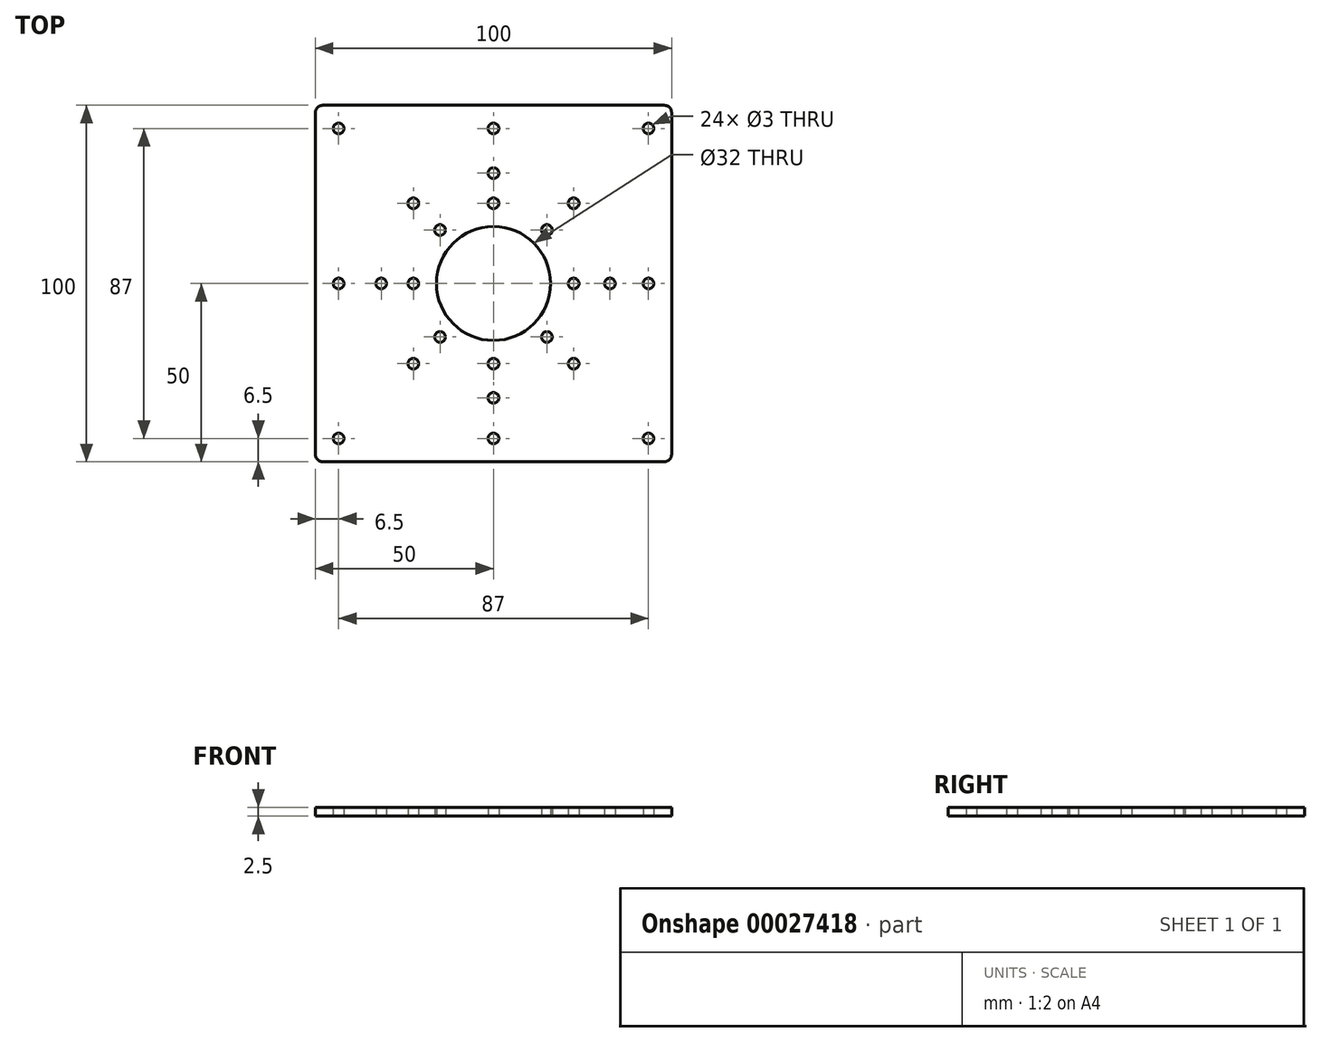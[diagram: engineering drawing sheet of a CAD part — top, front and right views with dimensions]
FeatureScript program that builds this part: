
annotation { "Feature Type Name" : "Feature", "Feature Type Description" : "" }
export const myFeature = defineFeature(function(context is Context, id is Id, definition is map)
    precondition{}
    {
        {
            var Q0;
            Q0=qCreatedBy(makeId("Top.planeOp"),FACE);
            var sketch = newSketch(context, id + "F0", { "sketchPlane" : qUnion([Q0])});
            skLineSegment(sketch, "E0.rect.bottom", {"start": v(50, -50) * mm, "end": v(-50, -50) * mm});
            skLineSegment(sketch, "E0.rect.top", {"start": v(50, 50) * mm, "end": v(-50, 50) * mm});
            skLineSegment(sketch, "E0.rect.left", {"start": v(50, -50) * mm, "end": v(50, 50) * mm});
            skLineSegment(sketch, "E0.rect.right", {"start": v(-50, -50) * mm, "end": v(-50, 50) * mm});
            skPoint(sketch, "E0.rect.middle", {"position": v(0, 0) * mm});
            skCircle(sketch, "E1", {"center": v(0, 0) * mm, "radius": 16 * mm});
            skLineSegment(sketch, "E2", {"start": v(50, 45) * mm, "end": v(-50, 45) * mm, "construction": true});
            skLineSegment(sketch, "E3", {"start": v(-50, 0) * mm, "end": v(50, 0) * mm, "construction": true});
            skLineSegment(sketch, "E4", {"start": v(45, 50) * mm, "end": v(45, -50) * mm, "construction": true});
            skCircle(sketch, "E5", {"center": v(-43.5, -43.5) * mm, "radius": 1.5 * mm});
            skCircle(sketch, "E6.MirrorC", {"center": v(43.5, -43.5) * mm, "radius": 1.5 * mm});
            skCircle(sketch, "E7.MirrorC", {"center": v(43.5, 43.5) * mm, "radius": 1.5 * mm});
            skCircle(sketch, "E8.MirrorC", {"center": v(-43.5, 43.5) * mm, "radius": 1.5 * mm});
            skPoint(sketch, "E9.centerSnap0", {"position": v(0, 45) * mm});
            skLineSegment(sketch, "E10.rect.bottom", {"start": v(22.5, 22.5) * mm, "end": v(-22.5, 22.5) * mm, "construction": true});
            skLineSegment(sketch, "E10.rect.top", {"start": v(22.5, -22.5) * mm, "end": v(-22.5, -22.5) * mm, "construction": true});
            skLineSegment(sketch, "E10.rect.left", {"start": v(22.5, 22.5) * mm, "end": v(22.5, -22.5) * mm, "construction": true});
            skLineSegment(sketch, "E10.rect.right", {"start": v(-22.5, 22.5) * mm, "end": v(-22.5, -22.5) * mm, "construction": true});
            skCircle(sketch, "E11", {"center": v(22.5, 22.5) * mm, "radius": 1.5 * mm});
            skCircle(sketch, "E12.MirrorC", {"center": v(-22.5, 22.5) * mm, "radius": 1.5 * mm});
            skCircle(sketch, "E13.MirrorC", {"center": v(22.5, -22.5) * mm, "radius": 1.5 * mm});
            skCircle(sketch, "E14.MirrorC", {"center": v(-22.5, -22.5) * mm, "radius": 1.5 * mm});
            skCircle(sketch, "E15", {"center": v(0, 22.5) * mm, "radius": 1.5 * mm});
            skCircle(sketch, "E16", {"center": v(-22.5, 0) * mm, "radius": 1.5 * mm});
            skCircle(sketch, "E17", {"center": v(0, -22.5) * mm, "radius": 1.5 * mm});
            skCircle(sketch, "E18", {"center": v(22.5, 0) * mm, "radius": 1.5 * mm});
            skCircle(sketch, "E19", {"center": v(-43.5, 0) * mm, "radius": 1.5 * mm});
            skCircle(sketch, "E20", {"center": v(0, -43.5) * mm, "radius": 1.5 * mm});
            skCircle(sketch, "E21", {"center": v(43.5, 0) * mm, "radius": 1.5 * mm});
            skCircle(sketch, "E22", {"center": v(0, 43.5) * mm, "radius": 1.5 * mm});
            skLineSegment(sketch, "E23", {"start": v(0, 30.97) * mm, "end": v(-31.53, 0) * mm, "construction": true});
            skLineSegment(sketch, "E24", {"start": v(-31.53, 0) * mm, "end": v(0, -32.1) * mm, "construction": true});
            skLineSegment(sketch, "E25", {"start": v(0, -32.1) * mm, "end": v(32.68, 0) * mm, "construction": true});
            skLineSegment(sketch, "E26", {"start": v(32.68, 0) * mm, "end": v(0, 30.97) * mm, "construction": true});
            skCircle(sketch, "E27", {"center": v(0, 30.97) * mm, "radius": 1.5 * mm});
            skCircle(sketch, "E28", {"center": v(-31.53, 0) * mm, "radius": 1.5 * mm});
            skCircle(sketch, "E29", {"center": v(0, -32.1) * mm, "radius": 1.5 * mm});
            skCircle(sketch, "E30", {"center": v(32.68, 0) * mm, "radius": 1.5 * mm});
            skLineSegment(sketch, "E31.rect.bottom", {"start": v(15, -15) * mm, "end": v(-15, -15) * mm, "construction": true});
            skLineSegment(sketch, "E31.rect.top", {"start": v(15, 15) * mm, "end": v(-15, 15) * mm, "construction": true});
            skLineSegment(sketch, "E31.rect.left", {"start": v(15, -15) * mm, "end": v(15, 15) * mm, "construction": true});
            skLineSegment(sketch, "E31.rect.right", {"start": v(-15, -15) * mm, "end": v(-15, 15) * mm, "construction": true});
            skCircle(sketch, "E32", {"center": v(-15, 15) * mm, "radius": 1.5 * mm});
            skCircle(sketch, "E33.MirrorC", {"center": v(15, 15) * mm, "radius": 1.5 * mm});
            skCircle(sketch, "E34.MirrorC", {"center": v(-15, -15) * mm, "radius": 1.5 * mm});
            skCircle(sketch, "E35.MirrorC", {"center": v(15, -15) * mm, "radius": 1.5 * mm});
            skSolve(sketch);
        }
        {
            var Q0;
            Q0=makeQuery(id+"F0.imprint","IMPRINT",FACE,{"disambiguationData":[TD([[makeQuery(id+"F0.imprint","IMPRINT",EDGE,{"derivedFrom":sQuery(id+"F0.wireOp",EDGE,"E0.rect.bottom")}),-1.0]])]});
            extrude(context, id + "F1", {"entities" : qUnion([Q0]), "depth" : 2.5 * mm});
        }
        {
            var Q0;
            Q0=makeQuery(id+"F1.opExtrude","SWEPT_EDGE",EDGE,{"disambiguationData":[OSD([sQuery(id+"F0.wireOp",EDGE,"E0.rect.bottom"),sQuery(id+"F0.wireOp",EDGE,"E0.rect.left")])]});
            var Q1;
            Q1=makeQuery(id+"F1.opExtrude","SWEPT_EDGE",EDGE,{"disambiguationData":[OSD([sQuery(id+"F0.wireOp",EDGE,"E0.rect.top"),sQuery(id+"F0.wireOp",EDGE,"E0.rect.left")])]});
            var Q2;
            Q2=makeQuery(id+"F1.opExtrude","SWEPT_EDGE",EDGE,{"disambiguationData":[OSD([sQuery(id+"F0.wireOp",EDGE,"E0.rect.top"),sQuery(id+"F0.wireOp",EDGE,"E0.rect.right")])]});
            var Q3;
            Q3=makeQuery(id+"F1.opExtrude","SWEPT_EDGE",EDGE,{"disambiguationData":[OSD([sQuery(id+"F0.wireOp",EDGE,"E0.rect.bottom"),sQuery(id+"F0.wireOp",EDGE,"E0.rect.right")])]});
            fillet(context, id + "F2", {"entities" : qUnion([Q0, Q1, Q2, Q3]), "radius" : 2 * mm, "tangentPropagation" : true, "allowEdgeOverflow" : false});
        }
    });
